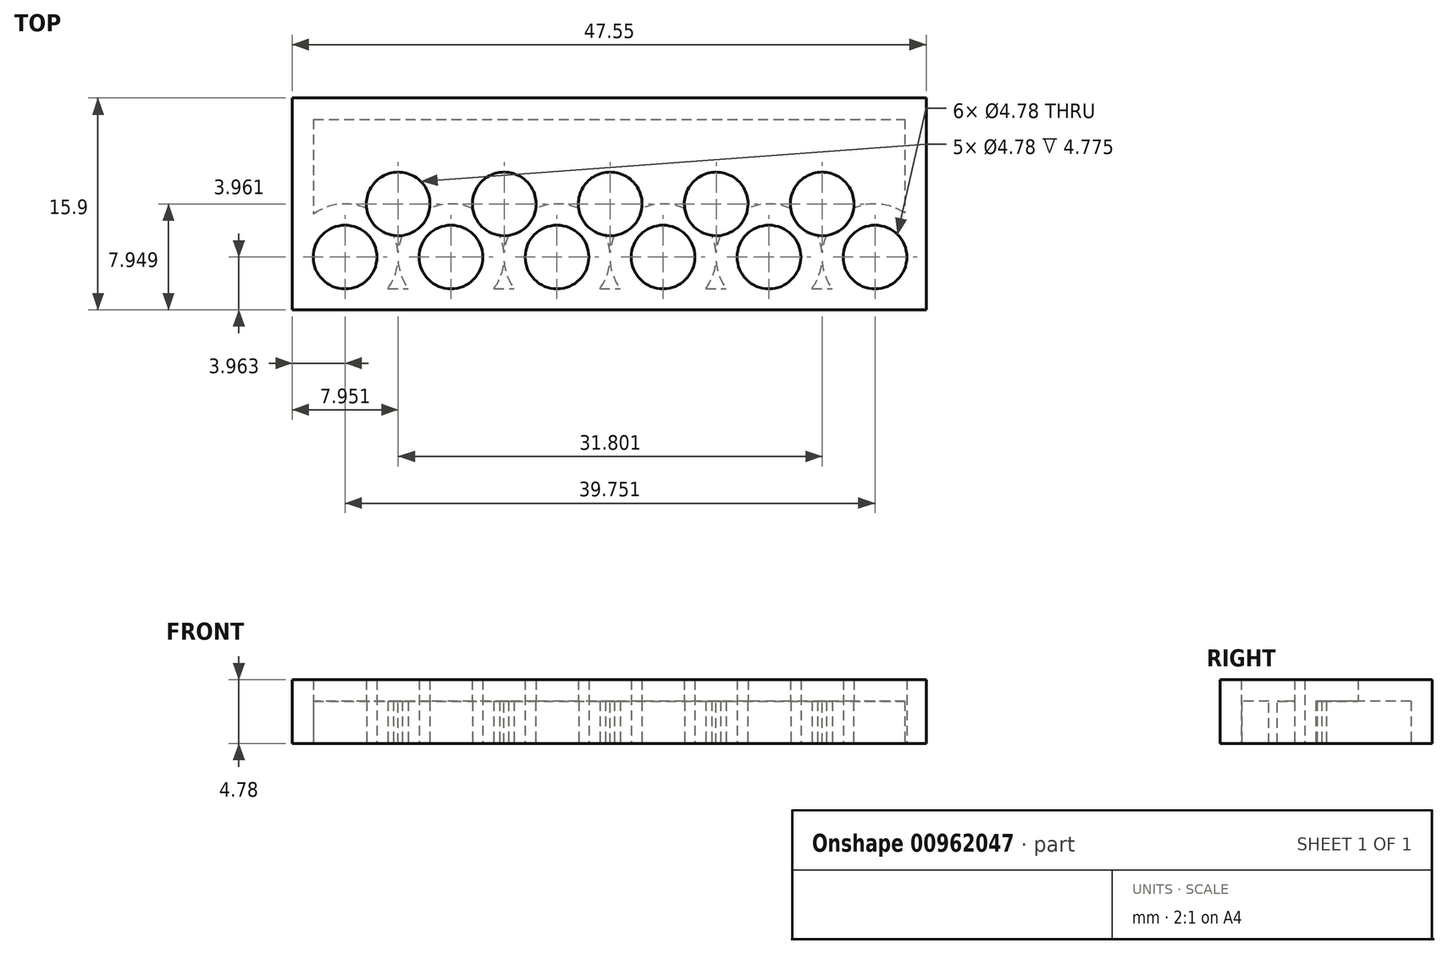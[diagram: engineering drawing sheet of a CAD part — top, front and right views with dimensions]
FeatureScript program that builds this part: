
annotation { "Feature Type Name" : "Feature", "Feature Type Description" : "" }
export const myFeature = defineFeature(function(context is Context, id is Id, definition is map)
    precondition{}
    {
        {
            var Q0;
            Q0=qCreatedBy(makeId("Top.planeOp"),FACE);
            var sketch = newSketch(context, id + "F0", { "sketchPlane" : qUnion([Q0])});
            skLineSegment(sketch, "E0.bottom", {"start": v(-6.1, 7.65) * mm, "end": v(41.44, 7.65) * mm});
            skLineSegment(sketch, "E0.top", {"start": v(-6.1, -8.25) * mm, "end": v(41.44, -8.25) * mm});
            skLineSegment(sketch, "E0.left", {"start": v(-6.1, 7.65) * mm, "end": v(-6.1, -8.25) * mm});
            skLineSegment(sketch, "E0.right", {"start": v(41.44, 7.65) * mm, "end": v(41.44, -8.25) * mm});
            skCircle(sketch, "E1", {"center": v(-2.15, 3.69) * mm, "radius": 2.39 * mm});
            skCircle(sketch, "E2.1.0.0", {"center": v(5.8, 3.69) * mm, "radius": 2.39 * mm});
            skCircle(sketch, "E2.2.0.0", {"center": v(13.75, 3.69) * mm, "radius": 2.39 * mm});
            skCircle(sketch, "E2.3.0.0", {"center": v(21.7, 3.69) * mm, "radius": 2.39 * mm});
            skCircle(sketch, "E2.4.0.0", {"center": v(29.65, 3.69) * mm, "radius": 2.39 * mm});
            skCircle(sketch, "E2.5.0.0", {"center": v(37.6, 3.69) * mm, "radius": 2.39 * mm});
            skLineSegment(sketch, "E2.direction1", {"start": v(-2.15, 3.69) * mm, "end": v(5.8, 3.69) * mm, "construction": true});
            skLineSegment(sketch, "E3", {"start": v(-6.1, -0.3) * mm, "end": v(41.44, -0.3) * mm, "construction": true});
            skCircle(sketch, "E4.MirrorC", {"center": v(-2.15, -4.29) * mm, "radius": 2.39 * mm});
            skCircle(sketch, "E5.MirrorC", {"center": v(5.8, -4.29) * mm, "radius": 2.39 * mm});
            skCircle(sketch, "E6.MirrorC", {"center": v(13.75, -4.29) * mm, "radius": 2.39 * mm});
            skCircle(sketch, "E7.MirrorC", {"center": v(21.7, -4.29) * mm, "radius": 2.39 * mm});
            skCircle(sketch, "E8.MirrorC", {"center": v(29.65, -4.29) * mm, "radius": 2.39 * mm});
            skCircle(sketch, "E9.MirrorC", {"center": v(37.6, -4.29) * mm, "radius": 2.39 * mm});
            skSolve(sketch);
        }
        {
            var Q0;
            Q0=makeQuery(id+"F0.imprint","IMPRINT",FACE,{"disambiguationData":[TD([[makeQuery(id+"F0.imprint","IMPRINT",EDGE,{"derivedFrom":sQuery(id+"F0.wireOp",EDGE,"E0.bottom")}),-1.0]])]});
            extrude(context, id + "F1", {"entities" : qUnion([Q0]), "depth" : 3.17 * mm, "offsetDistance" : 25.4 * mm});
        }
        {
            var Q0;
            Q0=makeQuery(id+"F0.imprint","IMPRINT",FACE,{"disambiguationData":[TD([[makeQuery(id+"F0.imprint","IMPRINT",EDGE,{"derivedFrom":sQuery(id+"F0.wireOp",EDGE,"E1")}),1.0]])]});
            var Q1;
            Q1=makeQuery(id+"F0.imprint","IMPRINT",FACE,{"disambiguationData":[TD([[makeQuery(id+"F0.imprint","IMPRINT",EDGE,{"derivedFrom":sQuery(id+"F0.wireOp",EDGE,"E2.1.0.0")}),1.0]])]});
            var Q2;
            Q2=makeQuery(id+"F0.imprint","IMPRINT",FACE,{"disambiguationData":[TD([[makeQuery(id+"F0.imprint","IMPRINT",EDGE,{"derivedFrom":sQuery(id+"F0.wireOp",EDGE,"E2.2.0.0")}),1.0]])]});
            var Q3;
            Q3=makeQuery(id+"F0.imprint","IMPRINT",FACE,{"disambiguationData":[TD([[makeQuery(id+"F0.imprint","IMPRINT",EDGE,{"derivedFrom":sQuery(id+"F0.wireOp",EDGE,"E2.3.0.0")}),1.0]])]});
            var Q4;
            Q4=makeQuery(id+"F0.imprint","IMPRINT",FACE,{"disambiguationData":[TD([[makeQuery(id+"F0.imprint","IMPRINT",EDGE,{"derivedFrom":sQuery(id+"F0.wireOp",EDGE,"E2.4.0.0")}),1.0]])]});
            var Q5;
            Q5=makeQuery(id+"F0.imprint","IMPRINT",FACE,{"disambiguationData":[TD([[makeQuery(id+"F0.imprint","IMPRINT",EDGE,{"derivedFrom":sQuery(id+"F0.wireOp",EDGE,"E2.5.0.0")}),1.0]])]});
            var Q6;
            Q6=makeQuery(id+"F0.imprint","IMPRINT",FACE,{"disambiguationData":[TD([[makeQuery(id+"F0.imprint","IMPRINT",EDGE,{"derivedFrom":sQuery(id+"F0.wireOp",EDGE,"E9.MirrorC")}),-1.0]])]});
            var Q7;
            Q7=makeQuery(id+"F0.imprint","IMPRINT",FACE,{"disambiguationData":[TD([[makeQuery(id+"F0.imprint","IMPRINT",EDGE,{"derivedFrom":sQuery(id+"F0.wireOp",EDGE,"E8.MirrorC")}),-1.0]])]});
            var Q8;
            Q8=makeQuery(id+"F0.imprint","IMPRINT",FACE,{"disambiguationData":[TD([[makeQuery(id+"F0.imprint","IMPRINT",EDGE,{"derivedFrom":sQuery(id+"F0.wireOp",EDGE,"E7.MirrorC")}),-1.0]])]});
            var Q9;
            Q9=makeQuery(id+"F0.imprint","IMPRINT",FACE,{"disambiguationData":[TD([[makeQuery(id+"F0.imprint","IMPRINT",EDGE,{"derivedFrom":sQuery(id+"F0.wireOp",EDGE,"E6.MirrorC")}),-1.0]])]});
            var Q10;
            Q10=makeQuery(id+"F0.imprint","IMPRINT",FACE,{"disambiguationData":[TD([[makeQuery(id+"F0.imprint","IMPRINT",EDGE,{"derivedFrom":sQuery(id+"F0.wireOp",EDGE,"E5.MirrorC")}),-1.0]])]});
            var Q11;
            Q11=makeQuery(id+"F0.imprint","IMPRINT",FACE,{"disambiguationData":[TD([[makeQuery(id+"F0.imprint","IMPRINT",EDGE,{"derivedFrom":sQuery(id+"F0.wireOp",EDGE,"E4.MirrorC")}),-1.0]])]});
            extrude(context, id + "F2", {"entities" : qUnion([Q0, Q1, Q2, Q3, Q4, Q5, Q6, Q7, Q8, Q9, Q10, Q11]), "operationType" : NewBodyOperationType.ADD, "depth" : 4.78 * mm, "offsetDistance" : 25.4 * mm});
        }
        {
            var Q0;
            {var subQ0=sQuery(id+"F0.wireOp",EDGE,"E9.MirrorC");var subQ1=sQuery(id+"F0.wireOp",EDGE,"E8.MirrorC");var subQ2=sQuery(id+"F0.wireOp",EDGE,"E7.MirrorC");var subQ3=sQuery(id+"F0.wireOp",EDGE,"E6.MirrorC");var subQ4=sQuery(id+"F0.wireOp",EDGE,"E5.MirrorC");var subQ5=sQuery(id+"F0.wireOp",EDGE,"E4.MirrorC");var subQ6=sQuery(id+"F0.wireOp",EDGE,"E2.5.0.0");var subQ7=sQuery(id+"F0.wireOp",EDGE,"E2.4.0.0");var subQ8=sQuery(id+"F0.wireOp",EDGE,"E2.3.0.0");var subQ9=sQuery(id+"F0.wireOp",EDGE,"E2.2.0.0");var subQ10=sQuery(id+"F0.wireOp",EDGE,"E2.1.0.0");var subQ11=sQuery(id+"F0.wireOp",EDGE,"E1");Q0=makeQuery(id+"F2.boolean.opBoolean","MERGE",FACE,{"derivedFrom":[makeQuery(id+"F1.opExtrude","CAP_FACE",FACE,{"disambiguationData":[OSD([sQuery(id+"F0.wireOp",EDGE,"E0.bottom"),sQuery(id+"F0.wireOp",EDGE,"E0.top"),sQuery(id+"F0.wireOp",EDGE,"E0.left"),sQuery(id+"F0.wireOp",EDGE,"E0.right"),subQ11,subQ10,subQ9,subQ8,subQ7,subQ6,subQ5,subQ4,subQ3,subQ2,subQ1,subQ0])],"isStart":true}),makeQuery(id+"F2.opExtrude","CAP_FACE",FACE,{"disambiguationData":[OSD([subQ11])],"isStart":true}),makeQuery(id+"F2.opExtrude","CAP_FACE",FACE,{"disambiguationData":[OSD([subQ10])],"isStart":true}),makeQuery(id+"F2.opExtrude","CAP_FACE",FACE,{"disambiguationData":[OSD([subQ9])],"isStart":true}),makeQuery(id+"F2.opExtrude","CAP_FACE",FACE,{"disambiguationData":[OSD([subQ8])],"isStart":true}),makeQuery(id+"F2.opExtrude","CAP_FACE",FACE,{"disambiguationData":[OSD([subQ7])],"isStart":true}),makeQuery(id+"F2.opExtrude","CAP_FACE",FACE,{"disambiguationData":[OSD([subQ6])],"isStart":true}),makeQuery(id+"F2.opExtrude","CAP_FACE",FACE,{"disambiguationData":[OSD([subQ5])],"isStart":true}),makeQuery(id+"F2.opExtrude","CAP_FACE",FACE,{"disambiguationData":[OSD([subQ4])],"isStart":true}),makeQuery(id+"F2.opExtrude","CAP_FACE",FACE,{"disambiguationData":[OSD([subQ3])],"isStart":true}),makeQuery(id+"F2.opExtrude","CAP_FACE",FACE,{"disambiguationData":[OSD([subQ2])],"isStart":true}),makeQuery(id+"F2.opExtrude","CAP_FACE",FACE,{"disambiguationData":[OSD([subQ1])],"isStart":true}),makeQuery(id+"F2.opExtrude","CAP_FACE",FACE,{"disambiguationData":[OSD([subQ0])],"isStart":true})]});}
            shell(context, id + "F3", {"entities" : qUnion([Q0]), "thickness" : 1.6 * mm});
        }
        {
            var Q0;
            Q0=makeQuery(id+"F0.imprint","IMPRINT",FACE,{"disambiguationData":[TD([[makeQuery(id+"F0.imprint","IMPRINT",EDGE,{"derivedFrom":sQuery(id+"F0.wireOp",EDGE,"E0.bottom")}),-1.0]])]});
            var sketch = newSketch(context, id + "F4", { "sketchPlane" : qUnion([Q0])});
            skCircle(sketch, "E10", {"center": v(1.84, -0.3) * mm, "radius": 2.39 * mm});
            skCircle(sketch, "E11.1.0.0", {"center": v(9.8, -0.3) * mm, "radius": 2.39 * mm});
            skCircle(sketch, "E11.2.0.0", {"center": v(17.74, -0.3) * mm, "radius": 2.39 * mm});
            skCircle(sketch, "E11.3.0.0", {"center": v(25.7, -0.3) * mm, "radius": 2.39 * mm});
            skCircle(sketch, "E11.4.0.0", {"center": v(33.64, -0.3) * mm, "radius": 2.39 * mm});
            skLineSegment(sketch, "E11.direction1", {"start": v(1.84, -0.3) * mm, "end": v(9.8, -0.3) * mm, "construction": true});
            skSolve(sketch);
        }
        {
            var Q0;
            Q0=makeQuery(id+"F4.imprint","IMPRINT",FACE,{"disambiguationData":[TD([[makeQuery(id+"F4.imprint","IMPRINT",EDGE,{"derivedFrom":sQuery(id+"F4.wireOp",EDGE,"E11.4.0.0")}),1.0]])]});
            var Q1;
            Q1=makeQuery(id+"F4.imprint","IMPRINT",FACE,{"disambiguationData":[TD([[makeQuery(id+"F4.imprint","IMPRINT",EDGE,{"derivedFrom":sQuery(id+"F4.wireOp",EDGE,"E11.3.0.0")}),1.0]])]});
            var Q2;
            Q2=makeQuery(id+"F4.imprint","IMPRINT",FACE,{"disambiguationData":[TD([[makeQuery(id+"F4.imprint","IMPRINT",EDGE,{"derivedFrom":sQuery(id+"F4.wireOp",EDGE,"E11.1.0.0")}),1.0]])]});
            var Q3;
            Q3=makeQuery(id+"F4.imprint","IMPRINT",FACE,{"disambiguationData":[TD([[makeQuery(id+"F4.imprint","IMPRINT",EDGE,{"derivedFrom":sQuery(id+"F4.wireOp",EDGE,"E11.2.0.0")}),1.0]])]});
            var Q4;
            Q4=makeQuery(id+"F4.imprint","IMPRINT",FACE,{"disambiguationData":[TD([[makeQuery(id+"F4.imprint","IMPRINT",EDGE,{"derivedFrom":sQuery(id+"F4.wireOp",EDGE,"E10")}),1.0]])]});
            extrude(context, id + "F5", {"entities" : qUnion([Q0, Q1, Q2, Q3, Q4]), "operationType" : NewBodyOperationType.REMOVE, "depth" : 6.58 * mm, "offsetDistance" : 25.4 * mm});
        }
    });
